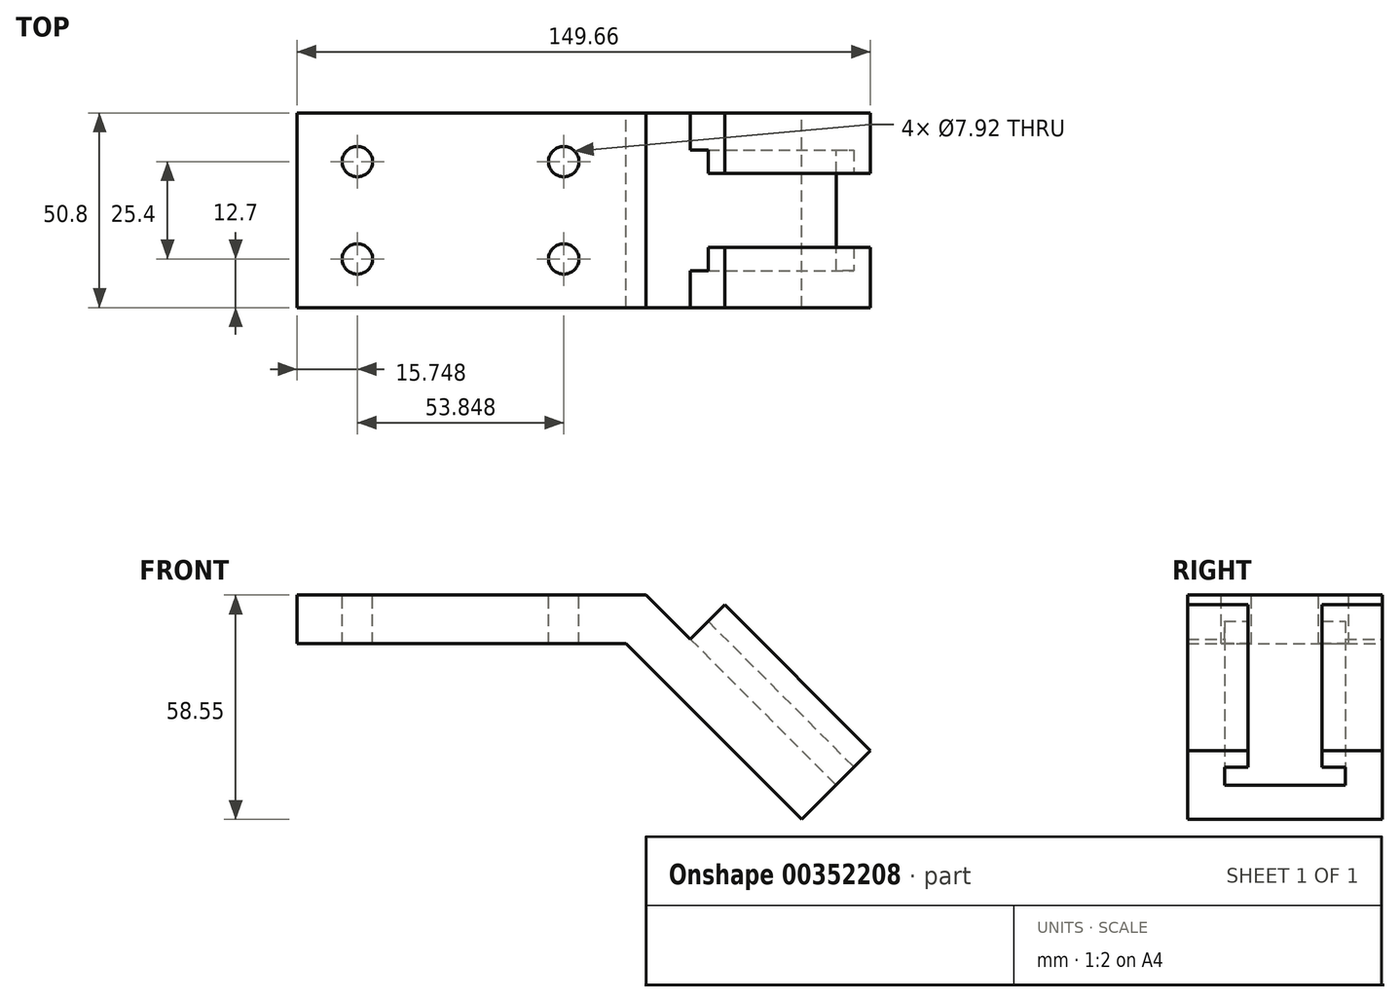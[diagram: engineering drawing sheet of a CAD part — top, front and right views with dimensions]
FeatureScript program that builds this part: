
annotation { "Feature Type Name" : "Feature", "Feature Type Description" : "" }
export const myFeature = defineFeature(function(context is Context, id is Id, definition is map)
    precondition{}
    {
        {
            var Q0;
            Q0=qCreatedBy(makeId("Front.planeOp"),FACE);
            var sketch = newSketch(context, id + "F0", { "sketchPlane" : qUnion([Q0])});
            skLineSegment(sketch, "E0.bottom", {"start": v(0, 0) * mm, "end": v(85.85, 0) * mm});
            skLineSegment(sketch, "E0.top", {"start": v(0, 12.7) * mm, "end": v(91.11, 12.7) * mm});
            skLineSegment(sketch, "E0.left", {"start": v(0, 0) * mm, "end": v(0, 12.7) * mm});
            skLineSegment(sketch, "E1", {"start": v(85.85, 0) * mm, "end": v(131.7, -45.85) * mm});
            skLineSegment(sketch, "E2", {"start": v(91.11, 12.7) * mm, "end": v(102.6, 1.2) * mm});
            skLineSegment(sketch, "E3", {"start": v(102.6, 1.2) * mm, "end": v(111.59, 10.19) * mm});
            skLineSegment(sketch, "E4", {"start": v(111.59, 10.19) * mm, "end": v(149.66, -27.9) * mm});
            skLineSegment(sketch, "E5", {"start": v(149.66, -27.9) * mm, "end": v(131.7, -45.85) * mm});
            skSolve(sketch);
        }
        {
            var Q0;
            Q0 = qSketchRegion(id + "F0", true);
            extrude(context, id + "F1", {"entities" : qUnion([Q0]), "endBound" : BoundingType.SYMMETRIC, "depth" : 50.8 * mm});
        }
        {
            var Q0;
            Q0=makeQuery(id+"F1.opExtrude","SWEPT_FACE",FACE,{"disambiguationData":[OSD([sQuery(id+"F0.wireOp",EDGE,"E5")])]});
            var sketch = newSketch(context, id + "F2", { "sketchPlane" : qUnion([Q0])});
            skLineSegment(sketch, "E6.0", {"start": v(-9.65, 86.1) * mm, "end": v(9.65, 86.1) * mm});
            skLineSegment(sketch, "E7", {"start": v(-9.65, 86.1) * mm, "end": v(-9.65, 80.01) * mm});
            skLineSegment(sketch, "E8", {"start": v(-9.65, 80.01) * mm, "end": v(-15.75, 80.01) * mm});
            skLineSegment(sketch, "E9", {"start": v(-15.75, 80.01) * mm, "end": v(-15.75, 73.4) * mm});
            skLineSegment(sketch, "E10", {"start": v(-15.75, 73.4) * mm, "end": v(15.75, 73.4) * mm});
            skLineSegment(sketch, "E11", {"start": v(15.75, 73.4) * mm, "end": v(15.75, 80.01) * mm});
            skLineSegment(sketch, "E12", {"start": v(15.75, 80.01) * mm, "end": v(9.65, 80.01) * mm});
            skLineSegment(sketch, "E13", {"start": v(9.65, 80.01) * mm, "end": v(9.65, 86.1) * mm});
            skPoint(sketch, "E14.orphan", {"position": v(-25.4, 86.1) * mm});
            skPoint(sketch, "E15.orphan", {"position": v(25.4, 86.1) * mm});
            skSolve(sketch);
        }
        {
            var Q0;
            Q0 = qSketchRegion(id + "F2", true);
            extrude(context, id + "F3", {"entities" : qUnion([Q0]), "operationType" : NewBodyOperationType.REMOVE, "endBound" : BoundingType.THROUGH_ALL, "oppositeDirection" : true, "depth" : 25.4 * mm});
        }
        {
            var Q0;
            {var subQ1=sQuery(id+"F0.wireOp",EDGE,"E4");Q0=makeQuery(id+"F3.boolean.opBoolean","SPLIT",FACE,{"disambiguationData":[TD([makeQuery(id+"F3.opExtrude","SWEPT_FACE",FACE,{"disambiguationData":[OSD([sQuery(id+"F2.wireOp",EDGE,"E13")])]})])],"derivedFrom":makeQuery(id+"F1.opExtrude","SWEPT_FACE",FACE,{"disambiguationData":[OSD([subQ1])]})});}
            var sketch = newSketch(context, id + "F4", { "sketchPlane" : qUnion([Q0])});
            skPoint(sketch, "E16.0", {"position": v(125.55, 0) * mm});
            skLineSegment(sketch, "E17.0", {"start": v(125.55, 0) * mm, "end": v(125.55, 0) * mm});
            skArc(sketch, "E18", {"start": v(119.18, -25.4) * mm, "mid": v(125.55, 0) * mm, "end": v(119.18, 25.4) * mm});
            skLineSegment(sketch, "E19", {"start": v(119.18, -25.4) * mm, "end": v(119.18, -33.22) * mm});
            skLineSegment(sketch, "E20", {"start": v(119.18, -33.22) * mm, "end": v(139.84, -33.22) * mm});
            skLineSegment(sketch, "E21", {"start": v(139.84, -33.22) * mm, "end": v(139.84, 34.85) * mm});
            skLineSegment(sketch, "E22", {"start": v(139.84, 34.85) * mm, "end": v(119.18, 34.85) * mm});
            skLineSegment(sketch, "E23", {"start": v(119.18, 34.85) * mm, "end": v(119.18, 25.4) * mm});
            skPoint(sketch, "E24.orphan", {"position": v(71.7, -25.4) * mm});
            skPoint(sketch, "E25.orphan", {"position": v(71.7, 25.4) * mm});
            skPoint(sketch, "E26.0.end.orphan", {"position": v(125.55, -25.4) * mm});
            skSolve(sketch);
        }
        {
            var Q0;
            Q0 = qSketchRegion(id + "F4", true);
            extrude(context, id + "F5", {"entities" : qUnion([Q0]), "operationType" : NewBodyOperationType.REMOVE, "endBound" : BoundingType.THROUGH_ALL, "oppositeDirection" : true, "depth" : 25.4 * mm});
        }
        {
            var Q0;
            Q0=makeQuery(id+"F1.opExtrude","SWEPT_FACE",FACE,{"disambiguationData":[OSD([sQuery(id+"F0.wireOp",EDGE,"E0.top")])]});
            var sketch = newSketch(context, id + "F6", { "sketchPlane" : qUnion([Q0])});
            skLineSegment(sketch, "E27", {"start": v(0, 0) * mm, "end": v(146.1, 0) * mm, "construction": true});
            skPoint(sketch, "E27.endSnap0", {"position": v(0, 0) * mm});
            skCircle(sketch, "E28", {"center": v(15.75, 12.7) * mm, "radius": 3.96 * mm});
            skCircle(sketch, "E29", {"center": v(15.75, -12.7) * mm, "radius": 3.96 * mm});
            skCircle(sketch, "E30", {"center": v(69.6, -12.7) * mm, "radius": 3.96 * mm});
            skCircle(sketch, "E31", {"center": v(69.6, 12.7) * mm, "radius": 3.96 * mm});
            skSolve(sketch);
        }
        {
            var Q0;
            Q0 = qSketchRegion(id + "F6", true);
            extrude(context, id + "F7", {"entities" : qUnion([Q0]), "operationType" : NewBodyOperationType.REMOVE, "endBound" : BoundingType.THROUGH_ALL, "oppositeDirection" : true, "depth" : 25.4 * mm});
        }
    });
